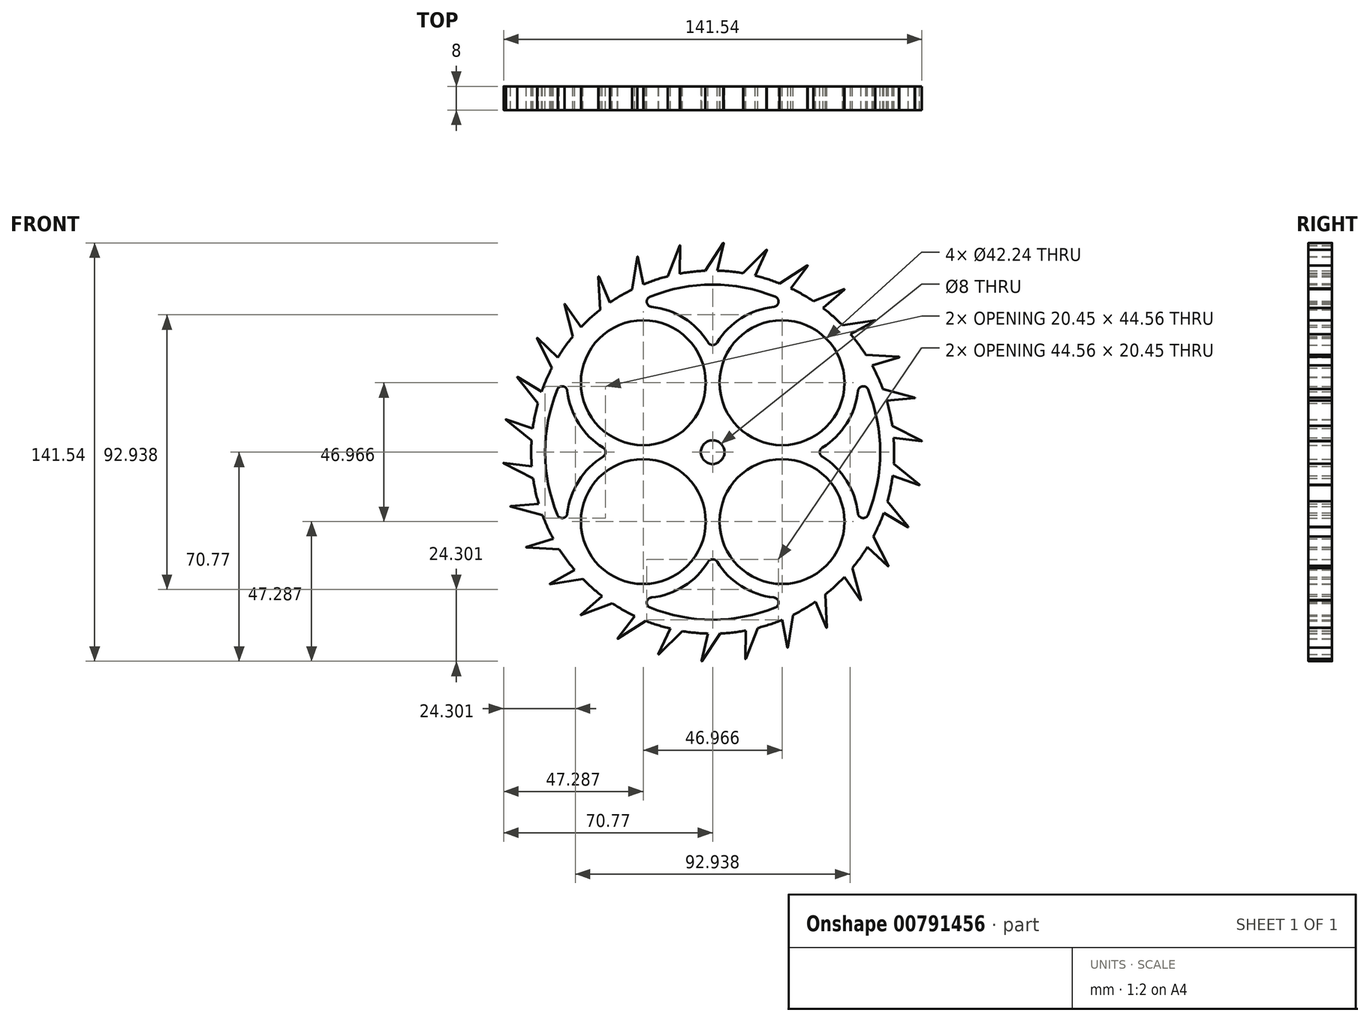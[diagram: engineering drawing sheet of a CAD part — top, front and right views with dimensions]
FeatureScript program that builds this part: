
annotation { "Feature Type Name" : "Feature", "Feature Type Description" : "" }
export const myFeature = defineFeature(function(context is Context, id is Id, definition is map)
    precondition{}
    {
        {
            var Q0;
            Q0=qCreatedBy(makeId("Front.planeOp"),FACE);
            var sketch = newSketch(context, id + "F0", { "sketchPlane" : qUnion([Q0])});
            skLineSegment(sketch, "E0", {"start": v(-50.01, 50.09) * mm, "end": v(-44.56, 42.27) * mm});
            skLineSegment(sketch, "E1", {"start": v(-50.14, 50.02) * mm, "end": v(-47.28, 39.2) * mm});
            skArc(sketch, "E2", {"start": v(-15.22, 59.5) * mm, "mid": v(-19.41, 58.27) * mm, "end": v(-23.51, 56.74) * mm});
            skCircle(sketch, "E3", {"center": v(23.48, 23.48) * mm, "radius": 21.12 * mm});
            skCircle(sketch, "E4", {"center": v(23.48, -23.48) * mm, "radius": 21.12 * mm});
            skCircle(sketch, "E5", {"center": v(-23.48, -23.48) * mm, "radius": 21.12 * mm});
            skCircle(sketch, "E6", {"center": v(-23.48, 23.48) * mm, "radius": 21.12 * mm});
            skArc(sketch, "E7", {"start": v(49.18, -20.72) * mm, "mid": v(45.35, -9.71) * mm, "end": v(37.08, -1.5) * mm});
            skArc(sketch, "E8", {"start": v(37.08, 1.5) * mm, "mid": v(45.35, 9.71) * mm, "end": v(49.18, 20.72) * mm});
            skArc(sketch, "E9", {"start": v(52.58, -21.19) * mm, "mid": v(56.7, 0) * mm, "end": v(52.58, 21.19) * mm});
            skArc(sketch, "E10", {"start": v(49.18, -20.72) * mm, "mid": v(50.7, -22.28) * mm, "end": v(52.58, -21.19) * mm});
            skArc(sketch, "E11", {"start": v(52.58, 21.19) * mm, "mid": v(50.7, 22.28) * mm, "end": v(49.18, 20.72) * mm});
            skArc(sketch, "E12", {"start": v(37.08, 1.5) * mm, "mid": v(36.25, 0) * mm, "end": v(37.08, -1.5) * mm});
            skArc(sketch, "E13", {"start": v(20.72, 49.18) * mm, "mid": v(22.28, 50.7) * mm, "end": v(21.19, 52.58) * mm});
            skArc(sketch, "E14", {"start": v(-21.19, 52.58) * mm, "mid": v(-22.28, 50.7) * mm, "end": v(-20.72, 49.18) * mm});
            skArc(sketch, "E15", {"start": v(-1.5, 37.08) * mm, "mid": v(0, 36.25) * mm, "end": v(1.5, 37.08) * mm});
            skArc(sketch, "E16", {"start": v(21.19, 52.58) * mm, "mid": v(0, 56.7) * mm, "end": v(-21.19, 52.58) * mm});
            skArc(sketch, "E17", {"start": v(-1.5, 37.08) * mm, "mid": v(-9.71, 45.35) * mm, "end": v(-20.72, 49.18) * mm});
            skArc(sketch, "E18", {"start": v(20.72, 49.18) * mm, "mid": v(9.71, 45.35) * mm, "end": v(1.5, 37.08) * mm});
            skArc(sketch, "E19", {"start": v(-49.18, 20.72) * mm, "mid": v(-50.7, 22.28) * mm, "end": v(-52.58, 21.19) * mm});
            skArc(sketch, "E20", {"start": v(-52.58, -21.19) * mm, "mid": v(-50.7, -22.28) * mm, "end": v(-49.18, -20.72) * mm});
            skArc(sketch, "E21", {"start": v(-37.08, -1.5) * mm, "mid": v(-36.25, 0) * mm, "end": v(-37.08, 1.5) * mm});
            skArc(sketch, "E22", {"start": v(-52.58, 21.19) * mm, "mid": v(-56.7, 0) * mm, "end": v(-52.58, -21.19) * mm});
            skArc(sketch, "E23", {"start": v(-37.08, -1.5) * mm, "mid": v(-45.35, -9.71) * mm, "end": v(-49.18, -20.72) * mm});
            skArc(sketch, "E24", {"start": v(-49.18, 20.72) * mm, "mid": v(-45.35, 9.71) * mm, "end": v(-37.08, 1.5) * mm});
            skArc(sketch, "E25", {"start": v(-20.72, -49.18) * mm, "mid": v(-22.28, -50.7) * mm, "end": v(-21.19, -52.58) * mm});
            skArc(sketch, "E26", {"start": v(21.19, -52.58) * mm, "mid": v(22.28, -50.7) * mm, "end": v(20.72, -49.18) * mm});
            skArc(sketch, "E27", {"start": v(1.5, -37.08) * mm, "mid": v(0, -36.25) * mm, "end": v(-1.5, -37.08) * mm});
            skArc(sketch, "E28", {"start": v(-21.19, -52.58) * mm, "mid": v(0, -56.7) * mm, "end": v(21.19, -52.58) * mm});
            skArc(sketch, "E29", {"start": v(1.5, -37.08) * mm, "mid": v(9.71, -45.35) * mm, "end": v(20.72, -49.18) * mm});
            skArc(sketch, "E30", {"start": v(-20.72, -49.18) * mm, "mid": v(-9.71, -45.35) * mm, "end": v(-1.5, -37.08) * mm});
            skArc(sketch, "E31", {"start": v(-50.01, 50.09) * mm, "mid": v(-50.1, 50.1) * mm, "end": v(-50.14, 50.02) * mm});
            skLineSegment(sketch, "E32", {"start": v(-59.44, 38.5) * mm, "end": v(-54.4, 28.5) * mm});
            skArc(sketch, "E33", {"start": v(-59.33, 38.6) * mm, "mid": v(-59.43, 38.6) * mm, "end": v(-59.44, 38.5) * mm});
            skLineSegment(sketch, "E34", {"start": v(-59.33, 38.6) * mm, "end": v(-52.37, 32.08) * mm});
            skLineSegment(sketch, "E35", {"start": v(-66.15, 25.3) * mm, "end": v(-59.14, 16.57) * mm});
            skArc(sketch, "E36", {"start": v(-66.06, 25.41) * mm, "mid": v(-66.16, 25.4) * mm, "end": v(-66.15, 25.3) * mm});
            skLineSegment(sketch, "E37", {"start": v(-66.06, 25.41) * mm, "end": v(-57.9, 20.5) * mm});
            skLineSegment(sketch, "E38", {"start": v(-69.97, 11) * mm, "end": v(-61.3, 3.92) * mm});
            skArc(sketch, "E39", {"start": v(-69.9, 11.12) * mm, "mid": v(-69.99, 11.09) * mm, "end": v(-69.97, 11) * mm});
            skLineSegment(sketch, "E40", {"start": v(-69.9, 11.12) * mm, "end": v(-60.9, 8) * mm});
            skLineSegment(sketch, "E41", {"start": v(-70.72, -3.8) * mm, "end": v(-60.77, -8.91) * mm});
            skArc(sketch, "E42", {"start": v(-70.69, -3.65) * mm, "mid": v(-70.77, -3.7) * mm, "end": v(-70.72, -3.8) * mm});
            skLineSegment(sketch, "E43", {"start": v(-70.69, -3.65) * mm, "end": v(-61.23, -4.83) * mm});
            skLineSegment(sketch, "E44", {"start": v(-68.39, -18.41) * mm, "end": v(-57.59, -21.35) * mm});
            skArc(sketch, "E45", {"start": v(-68.38, -18.27) * mm, "mid": v(-68.45, -18.34) * mm, "end": v(-68.39, -18.41) * mm});
            skLineSegment(sketch, "E46", {"start": v(-68.38, -18.27) * mm, "end": v(-58.89, -17.45) * mm});
            skLineSegment(sketch, "E47", {"start": v(-63.06, -32.23) * mm, "end": v(-51.89, -32.86) * mm});
            skArc(sketch, "E48", {"start": v(-63.09, -32.09) * mm, "mid": v(-63.14, -32.17) * mm, "end": v(-63.06, -32.23) * mm});
            skLineSegment(sketch, "E49", {"start": v(-63.09, -32.09) * mm, "end": v(-53.97, -29.31) * mm});
            skLineSegment(sketch, "E50", {"start": v(-54.99, -44.64) * mm, "end": v(-43.92, -42.93) * mm});
            skArc(sketch, "E51", {"start": v(-55.04, -44.5) * mm, "mid": v(-55.07, -44.6) * mm, "end": v(-54.99, -44.64) * mm});
            skLineSegment(sketch, "E52", {"start": v(-55.04, -44.5) * mm, "end": v(-46.7, -39.9) * mm});
            skLineSegment(sketch, "E53", {"start": v(-44.5, -55.1) * mm, "end": v(-34.04, -51.12) * mm});
            skArc(sketch, "E54", {"start": v(-44.58, -54.97) * mm, "mid": v(-44.6, -55.07) * mm, "end": v(-44.5, -55.1) * mm});
            skLineSegment(sketch, "E55", {"start": v(-44.58, -54.97) * mm, "end": v(-37.38, -48.73) * mm});
            skLineSegment(sketch, "E56", {"start": v(-32.08, -63.14) * mm, "end": v(-22.66, -57.08) * mm});
            skArc(sketch, "E57", {"start": v(-32.18, -63.04) * mm, "mid": v(-32.17, -63.14) * mm, "end": v(-32.08, -63.14) * mm});
            skLineSegment(sketch, "E58", {"start": v(-32.18, -63.04) * mm, "end": v(-26.43, -55.44) * mm});
            skLineSegment(sketch, "E59", {"start": v(-18.25, -68.43) * mm, "end": v(-10.3, -60.55) * mm});
            skArc(sketch, "E60", {"start": v(-18.37, -68.35) * mm, "mid": v(-18.34, -68.45) * mm, "end": v(-18.25, -68.43) * mm});
            skLineSegment(sketch, "E61", {"start": v(-18.37, -68.35) * mm, "end": v(-14.33, -59.72) * mm});
            skLineSegment(sketch, "E62", {"start": v(-3.62, -70.73) * mm, "end": v(2.51, -61.37) * mm});
            skArc(sketch, "E63", {"start": v(-3.76, -70.68) * mm, "mid": v(-3.71, -70.77) * mm, "end": v(-3.62, -70.73) * mm});
            skLineSegment(sketch, "E64", {"start": v(-3.76, -70.68) * mm, "end": v(-1.6, -61.4) * mm});
            skLineSegment(sketch, "E65", {"start": v(11.16, -69.94) * mm, "end": v(15.22, -59.5) * mm});
            skArc(sketch, "E66", {"start": v(11.02, -69.92) * mm, "mid": v(11.08, -70) * mm, "end": v(11.16, -69.94) * mm});
            skLineSegment(sketch, "E67", {"start": v(11.02, -69.92) * mm, "end": v(11.2, -60.39) * mm});
            skLineSegment(sketch, "E68", {"start": v(25.46, -66.09) * mm, "end": v(27.25, -55.04) * mm});
            skArc(sketch, "E69", {"start": v(25.32, -66.1) * mm, "mid": v(25.4, -66.16) * mm, "end": v(25.46, -66.09) * mm});
            skLineSegment(sketch, "E70", {"start": v(25.32, -66.1) * mm, "end": v(23.51, -56.74) * mm});
            skLineSegment(sketch, "E71", {"start": v(38.65, -59.35) * mm, "end": v(38.1, -48.17) * mm});
            skArc(sketch, "E72", {"start": v(38.5, -59.39) * mm, "mid": v(38.6, -59.43) * mm, "end": v(38.65, -59.35) * mm});
            skLineSegment(sketch, "E73", {"start": v(38.5, -59.39) * mm, "end": v(34.8, -50.61) * mm});
            skLineSegment(sketch, "E74", {"start": v(50.14, -50.02) * mm, "end": v(47.28, -39.2) * mm});
            skArc(sketch, "E75", {"start": v(50.01, -50.09) * mm, "mid": v(50.1, -50.1) * mm, "end": v(50.14, -50.02) * mm});
            skLineSegment(sketch, "E76", {"start": v(50.01, -50.09) * mm, "end": v(44.56, -42.27) * mm});
            skLineSegment(sketch, "E77", {"start": v(59.44, -38.5) * mm, "end": v(54.4, -28.5) * mm});
            skArc(sketch, "E78", {"start": v(59.33, -38.6) * mm, "mid": v(59.43, -38.6) * mm, "end": v(59.44, -38.5) * mm});
            skLineSegment(sketch, "E79", {"start": v(59.33, -38.6) * mm, "end": v(52.37, -32.08) * mm});
            skLineSegment(sketch, "E80", {"start": v(66.15, -25.3) * mm, "end": v(59.14, -16.57) * mm});
            skArc(sketch, "E81", {"start": v(66.06, -25.41) * mm, "mid": v(66.16, -25.4) * mm, "end": v(66.15, -25.3) * mm});
            skLineSegment(sketch, "E82", {"start": v(66.06, -25.41) * mm, "end": v(57.9, -20.5) * mm});
            skLineSegment(sketch, "E83", {"start": v(69.97, -11) * mm, "end": v(61.3, -3.92) * mm});
            skArc(sketch, "E84", {"start": v(69.9, -11.12) * mm, "mid": v(69.99, -11.09) * mm, "end": v(69.97, -11) * mm});
            skLineSegment(sketch, "E85", {"start": v(69.9, -11.12) * mm, "end": v(60.9, -8) * mm});
            skLineSegment(sketch, "E86", {"start": v(70.72, 3.8) * mm, "end": v(60.77, 8.91) * mm});
            skArc(sketch, "E87", {"start": v(70.69, 3.65) * mm, "mid": v(70.77, 3.7) * mm, "end": v(70.72, 3.8) * mm});
            skLineSegment(sketch, "E88", {"start": v(70.69, 3.65) * mm, "end": v(61.23, 4.83) * mm});
            skLineSegment(sketch, "E89", {"start": v(68.39, 18.41) * mm, "end": v(57.59, 21.35) * mm});
            skArc(sketch, "E90", {"start": v(68.38, 18.27) * mm, "mid": v(68.45, 18.34) * mm, "end": v(68.39, 18.41) * mm});
            skLineSegment(sketch, "E91", {"start": v(68.38, 18.27) * mm, "end": v(58.89, 17.45) * mm});
            skLineSegment(sketch, "E92", {"start": v(63.06, 32.23) * mm, "end": v(51.89, 32.86) * mm});
            skArc(sketch, "E93", {"start": v(63.09, 32.09) * mm, "mid": v(63.14, 32.17) * mm, "end": v(63.06, 32.23) * mm});
            skLineSegment(sketch, "E94", {"start": v(63.09, 32.09) * mm, "end": v(53.97, 29.31) * mm});
            skLineSegment(sketch, "E95", {"start": v(54.99, 44.64) * mm, "end": v(43.92, 42.93) * mm});
            skArc(sketch, "E96", {"start": v(55.04, 44.5) * mm, "mid": v(55.07, 44.6) * mm, "end": v(54.99, 44.64) * mm});
            skLineSegment(sketch, "E97", {"start": v(55.04, 44.5) * mm, "end": v(46.7, 39.9) * mm});
            skLineSegment(sketch, "E98", {"start": v(44.5, 55.1) * mm, "end": v(34.04, 51.12) * mm});
            skArc(sketch, "E99", {"start": v(44.58, 54.97) * mm, "mid": v(44.6, 55.07) * mm, "end": v(44.5, 55.1) * mm});
            skLineSegment(sketch, "E100", {"start": v(44.58, 54.97) * mm, "end": v(37.38, 48.73) * mm});
            skLineSegment(sketch, "E101", {"start": v(32.08, 63.14) * mm, "end": v(22.66, 57.08) * mm});
            skArc(sketch, "E102", {"start": v(32.18, 63.04) * mm, "mid": v(32.17, 63.14) * mm, "end": v(32.08, 63.14) * mm});
            skLineSegment(sketch, "E103", {"start": v(32.18, 63.04) * mm, "end": v(26.43, 55.44) * mm});
            skLineSegment(sketch, "E104", {"start": v(18.25, 68.43) * mm, "end": v(10.3, 60.55) * mm});
            skArc(sketch, "E105", {"start": v(18.37, 68.35) * mm, "mid": v(18.34, 68.45) * mm, "end": v(18.25, 68.43) * mm});
            skLineSegment(sketch, "E106", {"start": v(18.37, 68.35) * mm, "end": v(14.33, 59.72) * mm});
            skLineSegment(sketch, "E107", {"start": v(3.62, 70.73) * mm, "end": v(-2.51, 61.37) * mm});
            skArc(sketch, "E108", {"start": v(3.76, 70.68) * mm, "mid": v(3.71, 70.77) * mm, "end": v(3.62, 70.73) * mm});
            skLineSegment(sketch, "E109", {"start": v(3.76, 70.68) * mm, "end": v(1.6, 61.4) * mm});
            skLineSegment(sketch, "E110", {"start": v(-11.16, 69.94) * mm, "end": v(-15.22, 59.5) * mm});
            skArc(sketch, "E111", {"start": v(-11.02, 69.92) * mm, "mid": v(-11.08, 70) * mm, "end": v(-11.16, 69.94) * mm});
            skLineSegment(sketch, "E112", {"start": v(-11.02, 69.92) * mm, "end": v(-11.2, 60.39) * mm});
            skLineSegment(sketch, "E113", {"start": v(-25.46, 66.09) * mm, "end": v(-27.25, 55.04) * mm});
            skArc(sketch, "E114", {"start": v(-25.32, 66.1) * mm, "mid": v(-25.4, 66.16) * mm, "end": v(-25.46, 66.09) * mm});
            skLineSegment(sketch, "E115", {"start": v(-25.32, 66.1) * mm, "end": v(-23.51, 56.74) * mm});
            skLineSegment(sketch, "E116", {"start": v(-38.65, 59.35) * mm, "end": v(-38.1, 48.17) * mm});
            skArc(sketch, "E117", {"start": v(-38.5, 59.39) * mm, "mid": v(-38.6, 59.43) * mm, "end": v(-38.65, 59.35) * mm});
            skLineSegment(sketch, "E118", {"start": v(-38.5, 59.39) * mm, "end": v(-34.8, 50.61) * mm});
            skArc(sketch, "E119", {"start": v(-27.25, 55.04) * mm, "mid": v(-31.1, 52.96) * mm, "end": v(-34.8, 50.61) * mm});
            skArc(sketch, "E120", {"start": v(-38.1, 48.17) * mm, "mid": v(-41.43, 45.34) * mm, "end": v(-44.56, 42.27) * mm});
            skArc(sketch, "E121", {"start": v(-47.28, 39.2) * mm, "mid": v(-49.95, 35.73) * mm, "end": v(-52.37, 32.08) * mm});
            skArc(sketch, "E122", {"start": v(-54.4, 28.5) * mm, "mid": v(-56.3, 24.56) * mm, "end": v(-57.9, 20.5) * mm});
            skArc(sketch, "E123", {"start": v(-59.14, 16.57) * mm, "mid": v(-60.17, 12.32) * mm, "end": v(-60.9, 8) * mm});
            skArc(sketch, "E124", {"start": v(-61.3, 3.92) * mm, "mid": v(-61.42, -0.46) * mm, "end": v(-61.23, -4.83) * mm});
            skArc(sketch, "E125", {"start": v(-60.77, -8.91) * mm, "mid": v(-59.98, -13.22) * mm, "end": v(-58.89, -17.45) * mm});
            skArc(sketch, "E126", {"start": v(-57.59, -21.35) * mm, "mid": v(-55.92, -25.4) * mm, "end": v(-53.97, -29.31) * mm});
            skArc(sketch, "E127", {"start": v(-51.89, -32.86) * mm, "mid": v(-49.42, -36.47) * mm, "end": v(-46.7, -39.9) * mm});
            skArc(sketch, "E128", {"start": v(-43.92, -42.93) * mm, "mid": v(-40.76, -45.95) * mm, "end": v(-37.38, -48.73) * mm});
            skArc(sketch, "E129", {"start": v(-34.04, -51.12) * mm, "mid": v(-30.31, -53.42) * mm, "end": v(-26.43, -55.44) * mm});
            skArc(sketch, "E130", {"start": v(-22.66, -57.08) * mm, "mid": v(-18.54, -58.55) * mm, "end": v(-14.33, -59.72) * mm});
            skArc(sketch, "E131", {"start": v(-10.3, -60.55) * mm, "mid": v(-5.97, -61.13) * mm, "end": v(-1.6, -61.4) * mm});
            skArc(sketch, "E132", {"start": v(2.51, -61.37) * mm, "mid": v(6.87, -61.03) * mm, "end": v(11.2, -60.39) * mm});
            skArc(sketch, "E133", {"start": v(15.22, -59.5) * mm, "mid": v(19.41, -58.27) * mm, "end": v(23.51, -56.74) * mm});
            skArc(sketch, "E134", {"start": v(27.25, -55.04) * mm, "mid": v(31.1, -52.96) * mm, "end": v(34.8, -50.61) * mm});
            skArc(sketch, "E135", {"start": v(38.1, -48.17) * mm, "mid": v(41.43, -45.34) * mm, "end": v(44.56, -42.27) * mm});
            skArc(sketch, "E136", {"start": v(47.28, -39.2) * mm, "mid": v(49.95, -35.73) * mm, "end": v(52.37, -32.08) * mm});
            skArc(sketch, "E137", {"start": v(54.4, -28.5) * mm, "mid": v(56.3, -24.56) * mm, "end": v(57.9, -20.5) * mm});
            skArc(sketch, "E138", {"start": v(59.14, -16.57) * mm, "mid": v(60.17, -12.32) * mm, "end": v(60.9, -8) * mm});
            skArc(sketch, "E139", {"start": v(61.3, -3.92) * mm, "mid": v(61.42, 0.46) * mm, "end": v(61.23, 4.83) * mm});
            skArc(sketch, "E140", {"start": v(60.77, 8.91) * mm, "mid": v(59.98, 13.22) * mm, "end": v(58.89, 17.45) * mm});
            skArc(sketch, "E141", {"start": v(57.59, 21.35) * mm, "mid": v(55.92, 25.4) * mm, "end": v(53.97, 29.31) * mm});
            skArc(sketch, "E142", {"start": v(51.89, 32.86) * mm, "mid": v(49.42, 36.47) * mm, "end": v(46.7, 39.9) * mm});
            skArc(sketch, "E143", {"start": v(43.92, 42.93) * mm, "mid": v(40.76, 45.95) * mm, "end": v(37.38, 48.73) * mm});
            skArc(sketch, "E144", {"start": v(34.04, 51.12) * mm, "mid": v(30.31, 53.42) * mm, "end": v(26.43, 55.44) * mm});
            skArc(sketch, "E145", {"start": v(22.66, 57.08) * mm, "mid": v(18.54, 58.55) * mm, "end": v(14.33, 59.72) * mm});
            skArc(sketch, "E146", {"start": v(10.3, 60.55) * mm, "mid": v(5.97, 61.13) * mm, "end": v(1.6, 61.4) * mm});
            skArc(sketch, "E147", {"start": v(-2.51, 61.37) * mm, "mid": v(-6.87, 61.03) * mm, "end": v(-11.2, 60.39) * mm});
            skSolve(sketch);
        }
        {
            var Q0;
            Q0=makeQuery(id+"F0.imprint","IMPRINT",FACE,{"disambiguationData":[TD([[makeQuery(id+"F0.imprint","IMPRINT",EDGE,{"derivedFrom":sQuery(id+"F0.wireOp",EDGE,"E0")}),-1.0]])]});
            extrude(context, id + "F1", {"entities" : qUnion([Q0]), "depth" : 8 * mm, "offsetDistance" : 25 * mm});
        }
        {
            var Q0;
            Q0=makeQuery(id+"F1.opExtrude","CAP_FACE",FACE,{"disambiguationData":[OSD([sQuery(id+"F0.wireOp",EDGE,"E0"),sQuery(id+"F0.wireOp",EDGE,"E1"),sQuery(id+"F0.wireOp",EDGE,"E2"),sQuery(id+"F0.wireOp",EDGE,"E3"),sQuery(id+"F0.wireOp",EDGE,"E4"),sQuery(id+"F0.wireOp",EDGE,"E5"),sQuery(id+"F0.wireOp",EDGE,"E6"),sQuery(id+"F0.wireOp",EDGE,"E7"),sQuery(id+"F0.wireOp",EDGE,"E8"),sQuery(id+"F0.wireOp",EDGE,"E9"),sQuery(id+"F0.wireOp",EDGE,"E10"),sQuery(id+"F0.wireOp",EDGE,"E11"),sQuery(id+"F0.wireOp",EDGE,"E12"),sQuery(id+"F0.wireOp",EDGE,"E13"),sQuery(id+"F0.wireOp",EDGE,"E14"),sQuery(id+"F0.wireOp",EDGE,"E15"),sQuery(id+"F0.wireOp",EDGE,"E16"),sQuery(id+"F0.wireOp",EDGE,"E17"),sQuery(id+"F0.wireOp",EDGE,"E18"),sQuery(id+"F0.wireOp",EDGE,"E19"),sQuery(id+"F0.wireOp",EDGE,"E20"),sQuery(id+"F0.wireOp",EDGE,"E21"),sQuery(id+"F0.wireOp",EDGE,"E22"),sQuery(id+"F0.wireOp",EDGE,"E23"),sQuery(id+"F0.wireOp",EDGE,"E24"),sQuery(id+"F0.wireOp",EDGE,"E25"),sQuery(id+"F0.wireOp",EDGE,"E26"),sQuery(id+"F0.wireOp",EDGE,"E27"),sQuery(id+"F0.wireOp",EDGE,"E28"),sQuery(id+"F0.wireOp",EDGE,"E29"),sQuery(id+"F0.wireOp",EDGE,"E30"),sQuery(id+"F0.wireOp",EDGE,"E31"),sQuery(id+"F0.wireOp",EDGE,"E32"),sQuery(id+"F0.wireOp",EDGE,"E33"),sQuery(id+"F0.wireOp",EDGE,"E34"),sQuery(id+"F0.wireOp",EDGE,"E35"),sQuery(id+"F0.wireOp",EDGE,"E36"),sQuery(id+"F0.wireOp",EDGE,"E37"),sQuery(id+"F0.wireOp",EDGE,"E38"),sQuery(id+"F0.wireOp",EDGE,"E39"),sQuery(id+"F0.wireOp",EDGE,"E40"),sQuery(id+"F0.wireOp",EDGE,"E41"),sQuery(id+"F0.wireOp",EDGE,"E42"),sQuery(id+"F0.wireOp",EDGE,"E43"),sQuery(id+"F0.wireOp",EDGE,"E44"),sQuery(id+"F0.wireOp",EDGE,"E45"),sQuery(id+"F0.wireOp",EDGE,"E46"),sQuery(id+"F0.wireOp",EDGE,"E47"),sQuery(id+"F0.wireOp",EDGE,"E48"),sQuery(id+"F0.wireOp",EDGE,"E49"),sQuery(id+"F0.wireOp",EDGE,"E50"),sQuery(id+"F0.wireOp",EDGE,"E51"),sQuery(id+"F0.wireOp",EDGE,"E52"),sQuery(id+"F0.wireOp",EDGE,"E53"),sQuery(id+"F0.wireOp",EDGE,"E54"),sQuery(id+"F0.wireOp",EDGE,"E55"),sQuery(id+"F0.wireOp",EDGE,"E56"),sQuery(id+"F0.wireOp",EDGE,"E57"),sQuery(id+"F0.wireOp",EDGE,"E58"),sQuery(id+"F0.wireOp",EDGE,"E59"),sQuery(id+"F0.wireOp",EDGE,"E60"),sQuery(id+"F0.wireOp",EDGE,"E61"),sQuery(id+"F0.wireOp",EDGE,"E62"),sQuery(id+"F0.wireOp",EDGE,"E63"),sQuery(id+"F0.wireOp",EDGE,"E64"),sQuery(id+"F0.wireOp",EDGE,"E65"),sQuery(id+"F0.wireOp",EDGE,"E66"),sQuery(id+"F0.wireOp",EDGE,"E67"),sQuery(id+"F0.wireOp",EDGE,"E68"),sQuery(id+"F0.wireOp",EDGE,"E69"),sQuery(id+"F0.wireOp",EDGE,"E70"),sQuery(id+"F0.wireOp",EDGE,"E71"),sQuery(id+"F0.wireOp",EDGE,"E72"),sQuery(id+"F0.wireOp",EDGE,"E73"),sQuery(id+"F0.wireOp",EDGE,"E74"),sQuery(id+"F0.wireOp",EDGE,"E75"),sQuery(id+"F0.wireOp",EDGE,"E76"),sQuery(id+"F0.wireOp",EDGE,"E77"),sQuery(id+"F0.wireOp",EDGE,"E78"),sQuery(id+"F0.wireOp",EDGE,"E79"),sQuery(id+"F0.wireOp",EDGE,"E80"),sQuery(id+"F0.wireOp",EDGE,"E81"),sQuery(id+"F0.wireOp",EDGE,"E82"),sQuery(id+"F0.wireOp",EDGE,"E83"),sQuery(id+"F0.wireOp",EDGE,"E84"),sQuery(id+"F0.wireOp",EDGE,"E85"),sQuery(id+"F0.wireOp",EDGE,"E86"),sQuery(id+"F0.wireOp",EDGE,"E87"),sQuery(id+"F0.wireOp",EDGE,"E88"),sQuery(id+"F0.wireOp",EDGE,"E89"),sQuery(id+"F0.wireOp",EDGE,"E90"),sQuery(id+"F0.wireOp",EDGE,"E91"),sQuery(id+"F0.wireOp",EDGE,"E92"),sQuery(id+"F0.wireOp",EDGE,"E93"),sQuery(id+"F0.wireOp",EDGE,"E94"),sQuery(id+"F0.wireOp",EDGE,"E95"),sQuery(id+"F0.wireOp",EDGE,"E96"),sQuery(id+"F0.wireOp",EDGE,"E97"),sQuery(id+"F0.wireOp",EDGE,"E98"),sQuery(id+"F0.wireOp",EDGE,"E99"),sQuery(id+"F0.wireOp",EDGE,"E100"),sQuery(id+"F0.wireOp",EDGE,"E101"),sQuery(id+"F0.wireOp",EDGE,"E102"),sQuery(id+"F0.wireOp",EDGE,"E103"),sQuery(id+"F0.wireOp",EDGE,"E104"),sQuery(id+"F0.wireOp",EDGE,"E105"),sQuery(id+"F0.wireOp",EDGE,"E106"),sQuery(id+"F0.wireOp",EDGE,"E107"),sQuery(id+"F0.wireOp",EDGE,"E108"),sQuery(id+"F0.wireOp",EDGE,"E109"),sQuery(id+"F0.wireOp",EDGE,"E110"),sQuery(id+"F0.wireOp",EDGE,"E111"),sQuery(id+"F0.wireOp",EDGE,"E112"),sQuery(id+"F0.wireOp",EDGE,"E113"),sQuery(id+"F0.wireOp",EDGE,"E114"),sQuery(id+"F0.wireOp",EDGE,"E115"),sQuery(id+"F0.wireOp",EDGE,"E116"),sQuery(id+"F0.wireOp",EDGE,"E117"),sQuery(id+"F0.wireOp",EDGE,"E118"),sQuery(id+"F0.wireOp",EDGE,"E119"),sQuery(id+"F0.wireOp",EDGE,"E120"),sQuery(id+"F0.wireOp",EDGE,"E121"),sQuery(id+"F0.wireOp",EDGE,"E122"),sQuery(id+"F0.wireOp",EDGE,"E123"),sQuery(id+"F0.wireOp",EDGE,"E124"),sQuery(id+"F0.wireOp",EDGE,"E125"),sQuery(id+"F0.wireOp",EDGE,"E126"),sQuery(id+"F0.wireOp",EDGE,"E127"),sQuery(id+"F0.wireOp",EDGE,"E128"),sQuery(id+"F0.wireOp",EDGE,"E129"),sQuery(id+"F0.wireOp",EDGE,"E130"),sQuery(id+"F0.wireOp",EDGE,"E131"),sQuery(id+"F0.wireOp",EDGE,"E132"),sQuery(id+"F0.wireOp",EDGE,"E133"),sQuery(id+"F0.wireOp",EDGE,"E134"),sQuery(id+"F0.wireOp",EDGE,"E135"),sQuery(id+"F0.wireOp",EDGE,"E136"),sQuery(id+"F0.wireOp",EDGE,"E137"),sQuery(id+"F0.wireOp",EDGE,"E138"),sQuery(id+"F0.wireOp",EDGE,"E139"),sQuery(id+"F0.wireOp",EDGE,"E140"),sQuery(id+"F0.wireOp",EDGE,"E141"),sQuery(id+"F0.wireOp",EDGE,"E142"),sQuery(id+"F0.wireOp",EDGE,"E143"),sQuery(id+"F0.wireOp",EDGE,"E144"),sQuery(id+"F0.wireOp",EDGE,"E145"),sQuery(id+"F0.wireOp",EDGE,"E146"),sQuery(id+"F0.wireOp",EDGE,"E147")])],"isStart":false});
            var sketch = newSketch(context, id + "F2", { "sketchPlane" : qUnion([Q0])});
            skPoint(sketch, "E148", {"position": v(0, 0) * mm});
            skSolve(sketch);
        }
        {
            var Q0;
            Q0=sQuery(id+"F2.wireOp",VERTEX,"E148");
            var Q1;
            Q1=makeQuery(id+"F1.opExtrude","SWEPT_BODY",BODY,{"disambiguationData":[OSD([sQuery(id+"F0.wireOp",EDGE,"E0"),sQuery(id+"F0.wireOp",EDGE,"E1"),sQuery(id+"F0.wireOp",EDGE,"E2"),sQuery(id+"F0.wireOp",EDGE,"E3"),sQuery(id+"F0.wireOp",EDGE,"E4"),sQuery(id+"F0.wireOp",EDGE,"E5"),sQuery(id+"F0.wireOp",EDGE,"E6"),sQuery(id+"F0.wireOp",EDGE,"E7"),sQuery(id+"F0.wireOp",EDGE,"E8"),sQuery(id+"F0.wireOp",EDGE,"E9"),sQuery(id+"F0.wireOp",EDGE,"E10"),sQuery(id+"F0.wireOp",EDGE,"E11"),sQuery(id+"F0.wireOp",EDGE,"E12"),sQuery(id+"F0.wireOp",EDGE,"E13"),sQuery(id+"F0.wireOp",EDGE,"E14"),sQuery(id+"F0.wireOp",EDGE,"E15"),sQuery(id+"F0.wireOp",EDGE,"E16"),sQuery(id+"F0.wireOp",EDGE,"E17"),sQuery(id+"F0.wireOp",EDGE,"E18"),sQuery(id+"F0.wireOp",EDGE,"E19"),sQuery(id+"F0.wireOp",EDGE,"E20"),sQuery(id+"F0.wireOp",EDGE,"E21"),sQuery(id+"F0.wireOp",EDGE,"E22"),sQuery(id+"F0.wireOp",EDGE,"E23"),sQuery(id+"F0.wireOp",EDGE,"E24"),sQuery(id+"F0.wireOp",EDGE,"E25"),sQuery(id+"F0.wireOp",EDGE,"E26"),sQuery(id+"F0.wireOp",EDGE,"E27"),sQuery(id+"F0.wireOp",EDGE,"E28"),sQuery(id+"F0.wireOp",EDGE,"E29"),sQuery(id+"F0.wireOp",EDGE,"E30"),sQuery(id+"F0.wireOp",EDGE,"E31"),sQuery(id+"F0.wireOp",EDGE,"E32"),sQuery(id+"F0.wireOp",EDGE,"E33"),sQuery(id+"F0.wireOp",EDGE,"E34"),sQuery(id+"F0.wireOp",EDGE,"E35"),sQuery(id+"F0.wireOp",EDGE,"E36"),sQuery(id+"F0.wireOp",EDGE,"E37"),sQuery(id+"F0.wireOp",EDGE,"E38"),sQuery(id+"F0.wireOp",EDGE,"E39"),sQuery(id+"F0.wireOp",EDGE,"E40"),sQuery(id+"F0.wireOp",EDGE,"E41"),sQuery(id+"F0.wireOp",EDGE,"E42"),sQuery(id+"F0.wireOp",EDGE,"E43"),sQuery(id+"F0.wireOp",EDGE,"E44"),sQuery(id+"F0.wireOp",EDGE,"E45"),sQuery(id+"F0.wireOp",EDGE,"E46"),sQuery(id+"F0.wireOp",EDGE,"E47"),sQuery(id+"F0.wireOp",EDGE,"E48"),sQuery(id+"F0.wireOp",EDGE,"E49"),sQuery(id+"F0.wireOp",EDGE,"E50"),sQuery(id+"F0.wireOp",EDGE,"E51"),sQuery(id+"F0.wireOp",EDGE,"E52"),sQuery(id+"F0.wireOp",EDGE,"E53"),sQuery(id+"F0.wireOp",EDGE,"E54"),sQuery(id+"F0.wireOp",EDGE,"E55"),sQuery(id+"F0.wireOp",EDGE,"E56"),sQuery(id+"F0.wireOp",EDGE,"E57"),sQuery(id+"F0.wireOp",EDGE,"E58"),sQuery(id+"F0.wireOp",EDGE,"E59"),sQuery(id+"F0.wireOp",EDGE,"E60"),sQuery(id+"F0.wireOp",EDGE,"E61"),sQuery(id+"F0.wireOp",EDGE,"E62"),sQuery(id+"F0.wireOp",EDGE,"E63"),sQuery(id+"F0.wireOp",EDGE,"E64"),sQuery(id+"F0.wireOp",EDGE,"E65"),sQuery(id+"F0.wireOp",EDGE,"E66"),sQuery(id+"F0.wireOp",EDGE,"E67"),sQuery(id+"F0.wireOp",EDGE,"E68"),sQuery(id+"F0.wireOp",EDGE,"E69"),sQuery(id+"F0.wireOp",EDGE,"E70"),sQuery(id+"F0.wireOp",EDGE,"E71"),sQuery(id+"F0.wireOp",EDGE,"E72"),sQuery(id+"F0.wireOp",EDGE,"E73"),sQuery(id+"F0.wireOp",EDGE,"E74"),sQuery(id+"F0.wireOp",EDGE,"E75"),sQuery(id+"F0.wireOp",EDGE,"E76"),sQuery(id+"F0.wireOp",EDGE,"E77"),sQuery(id+"F0.wireOp",EDGE,"E78"),sQuery(id+"F0.wireOp",EDGE,"E79"),sQuery(id+"F0.wireOp",EDGE,"E80"),sQuery(id+"F0.wireOp",EDGE,"E81"),sQuery(id+"F0.wireOp",EDGE,"E82"),sQuery(id+"F0.wireOp",EDGE,"E83"),sQuery(id+"F0.wireOp",EDGE,"E84"),sQuery(id+"F0.wireOp",EDGE,"E85"),sQuery(id+"F0.wireOp",EDGE,"E86"),sQuery(id+"F0.wireOp",EDGE,"E87"),sQuery(id+"F0.wireOp",EDGE,"E88"),sQuery(id+"F0.wireOp",EDGE,"E89"),sQuery(id+"F0.wireOp",EDGE,"E90"),sQuery(id+"F0.wireOp",EDGE,"E91"),sQuery(id+"F0.wireOp",EDGE,"E92"),sQuery(id+"F0.wireOp",EDGE,"E93"),sQuery(id+"F0.wireOp",EDGE,"E94"),sQuery(id+"F0.wireOp",EDGE,"E95"),sQuery(id+"F0.wireOp",EDGE,"E96"),sQuery(id+"F0.wireOp",EDGE,"E97"),sQuery(id+"F0.wireOp",EDGE,"E98"),sQuery(id+"F0.wireOp",EDGE,"E99"),sQuery(id+"F0.wireOp",EDGE,"E100"),sQuery(id+"F0.wireOp",EDGE,"E101"),sQuery(id+"F0.wireOp",EDGE,"E102"),sQuery(id+"F0.wireOp",EDGE,"E103"),sQuery(id+"F0.wireOp",EDGE,"E104"),sQuery(id+"F0.wireOp",EDGE,"E105"),sQuery(id+"F0.wireOp",EDGE,"E106"),sQuery(id+"F0.wireOp",EDGE,"E107"),sQuery(id+"F0.wireOp",EDGE,"E108"),sQuery(id+"F0.wireOp",EDGE,"E109"),sQuery(id+"F0.wireOp",EDGE,"E110"),sQuery(id+"F0.wireOp",EDGE,"E111"),sQuery(id+"F0.wireOp",EDGE,"E112"),sQuery(id+"F0.wireOp",EDGE,"E113"),sQuery(id+"F0.wireOp",EDGE,"E114"),sQuery(id+"F0.wireOp",EDGE,"E115"),sQuery(id+"F0.wireOp",EDGE,"E116"),sQuery(id+"F0.wireOp",EDGE,"E117"),sQuery(id+"F0.wireOp",EDGE,"E118"),sQuery(id+"F0.wireOp",EDGE,"E119"),sQuery(id+"F0.wireOp",EDGE,"E120"),sQuery(id+"F0.wireOp",EDGE,"E121"),sQuery(id+"F0.wireOp",EDGE,"E122"),sQuery(id+"F0.wireOp",EDGE,"E123"),sQuery(id+"F0.wireOp",EDGE,"E124"),sQuery(id+"F0.wireOp",EDGE,"E125"),sQuery(id+"F0.wireOp",EDGE,"E126"),sQuery(id+"F0.wireOp",EDGE,"E127"),sQuery(id+"F0.wireOp",EDGE,"E128"),sQuery(id+"F0.wireOp",EDGE,"E129"),sQuery(id+"F0.wireOp",EDGE,"E130"),sQuery(id+"F0.wireOp",EDGE,"E131"),sQuery(id+"F0.wireOp",EDGE,"E132"),sQuery(id+"F0.wireOp",EDGE,"E133"),sQuery(id+"F0.wireOp",EDGE,"E134"),sQuery(id+"F0.wireOp",EDGE,"E135"),sQuery(id+"F0.wireOp",EDGE,"E136"),sQuery(id+"F0.wireOp",EDGE,"E137"),sQuery(id+"F0.wireOp",EDGE,"E138"),sQuery(id+"F0.wireOp",EDGE,"E139"),sQuery(id+"F0.wireOp",EDGE,"E140"),sQuery(id+"F0.wireOp",EDGE,"E141"),sQuery(id+"F0.wireOp",EDGE,"E142"),sQuery(id+"F0.wireOp",EDGE,"E143"),sQuery(id+"F0.wireOp",EDGE,"E144"),sQuery(id+"F0.wireOp",EDGE,"E145"),sQuery(id+"F0.wireOp",EDGE,"E146"),sQuery(id+"F0.wireOp",EDGE,"E147")])]});
            hole(context, id + "F3", {"style" : HoleStyle.SIMPLE, "endStyle" : HoleEndStyle.THROUGH, "holeDiameter" : 8 * mm, "majorDiameter" : 5 * mm, "isTappedThrough" : true, "tappedDepth" : 12 * mm, "tapClearance" : 3, "locations" : qUnion([Q0]), "scope" : qUnion([Q1])});
        }
    });
